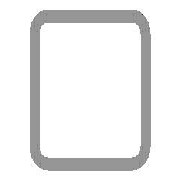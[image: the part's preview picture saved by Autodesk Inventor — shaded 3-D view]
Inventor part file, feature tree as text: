
AUTODESK INVENTOR PART (.ipt)
format: ipt  version: 2025 (Build 290162010, 162A)  size: 133,120 bytes
history: native  units: mm (DEFAULTED — no unit token found)
features: other x4, sketch x1, plane x1
ambient origin geometry x8: Origin, YZ Plane, XZ Plane, XY Plane, X Axis, Y Axis, Z Axis, Center Point
bodies: Solid1 (feature_tree), Body (feature_tree)
feature tree (6):
  parser-record x1  (decoder bookkeeping rows leaked as tree rows — omitted from the tree; the rows remain in map.json)
  other  "Driven Length"
  other  "Start Plane"
  other  "End Plane"
  sketch  "Sketch3"  dims[d3=2106.0mm d4=0.0mm d7=4.0mm d9=40.0mm d11=40.0mm d12=2.0mm d13=-0.0mm d14=2106.0mm d15=20.0mm d16=20.0mm d17=90.0deg d18=2106.0mm]
  plane  "Work Plane3"
